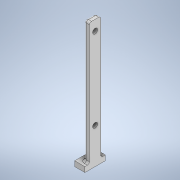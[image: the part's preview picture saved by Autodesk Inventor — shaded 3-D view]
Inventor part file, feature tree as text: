
AUTODESK INVENTOR PART (.ipt)
format: ipt  version: 2021.4 (Build 254397000, 397)  size: 138,752 bytes
history: native  units: mm
features: sketch x3, extrude x2, other x1, hole x1, fillet x1
ambient origin geometry x8: Origin, YZ Plane, XZ Plane, XY Plane, X Axis, Y Axis, Z Axis, Center Point
bodies: Body1 (feature_tree)
feature tree (8):
  other  "ソリッド1"
  extrude  "押し出し1"  Depth=10.0mm
  extrude  "押し出し4"  Depth=20.0mm
  hole  "穴2"  [1 undecoded]
  fillet  "フィレット3"  Radius=5.0mm
  sketch  "スケッチ1"
  sketch  "スケッチ4"
  sketch  "スケッチ6"
note: 1 required parameter value undecoded (feature->parameter linkage not recoverable at this tier; creation-order binding heuristic only, values carry confidence <= 0.55)
